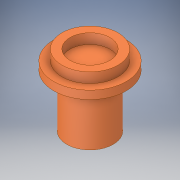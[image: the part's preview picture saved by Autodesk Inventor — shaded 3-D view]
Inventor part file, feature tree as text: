
AUTODESK INVENTOR PART (.ipt)
format: ipt  version: 2019.1 (Build 231200000, 200)  size: 135,680 bytes
history: mixed  units: in
note: dims shown in document units (in); Inventor stores cm internally (conversion verified against a paired STEP export)
features: revolve x1, imported_body x1
ambient origin geometry x8: Origin, YZ Plane, XZ Plane, XY Plane, X Axis, Y Axis, Z Axis, Center Point
bodies: Solid1 (imported_parasolid)
feature tree (2):
  revolve  "Revolve3"  [1 undecoded]
  imported_body  NMx_Import_Brep_tag  [imported B-rep: ~11 faces, bbox_mm=[0.0, 8.747963, 2.9]]
note: 1 required parameter value undecoded (feature->parameter linkage not recoverable at this tier; creation-order binding heuristic only, values carry confidence <= 0.55)
